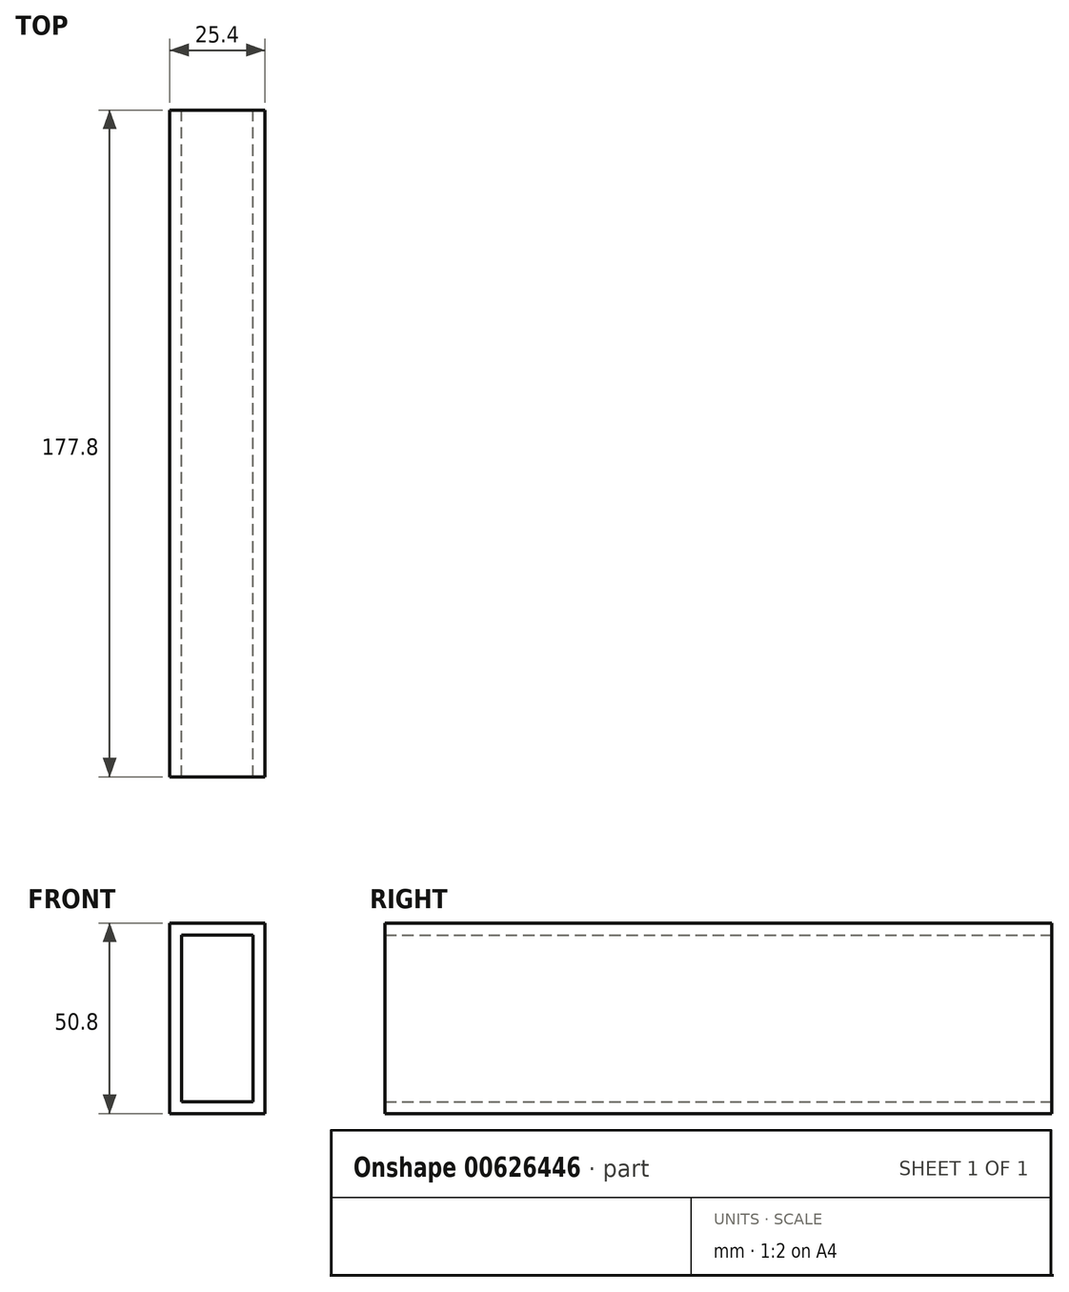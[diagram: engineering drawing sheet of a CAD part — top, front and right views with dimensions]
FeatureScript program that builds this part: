
annotation { "Feature Type Name" : "Feature", "Feature Type Description" : "" }
export const myFeature = defineFeature(function(context is Context, id is Id, definition is map)
    precondition{}
    {
        {
            var Q0;
            Q0=qCreatedBy(makeId("Front.planeOp"),FACE);
            var sketch = newSketch(context, id + "F0", { "sketchPlane" : qUnion([Q0])});
            skLineSegment(sketch, "E0.bottom", {"start": v(0, 0) * mm, "end": v(25.4, 0) * mm});
            skLineSegment(sketch, "E0.top", {"start": v(0, 50.8) * mm, "end": v(25.4, 50.8) * mm});
            skLineSegment(sketch, "E0.left", {"start": v(0, 0) * mm, "end": v(0, 50.8) * mm});
            skLineSegment(sketch, "E0.right", {"start": v(25.4, 0) * mm, "end": v(25.4, 50.8) * mm});
            skLineSegment(sketch, "E1.bottom", {"start": v(3.17, 47.63) * mm, "end": v(22.22, 47.63) * mm});
            skLineSegment(sketch, "E1.top", {"start": v(3.17, 3.18) * mm, "end": v(22.22, 3.18) * mm});
            skLineSegment(sketch, "E1.left", {"start": v(3.17, 47.63) * mm, "end": v(3.17, 3.18) * mm});
            skLineSegment(sketch, "E1.right", {"start": v(22.22, 47.63) * mm, "end": v(22.22, 3.18) * mm});
            skSolve(sketch);
        }
        {
            var Q0;
            Q0=makeQuery(id+"F0.imprint","IMPRINT",FACE,{"disambiguationData":[TD([[makeQuery(id+"F0.imprint","IMPRINT",EDGE,{"derivedFrom":sQuery(id+"F0.wireOp",EDGE,"E0.bottom")}),1.0]])]});
            extrude(context, id + "F1", {"entities" : qUnion([Q0]), "depth" : 177.8 * mm, "offsetDistance" : 25.4 * mm});
        }
    });
